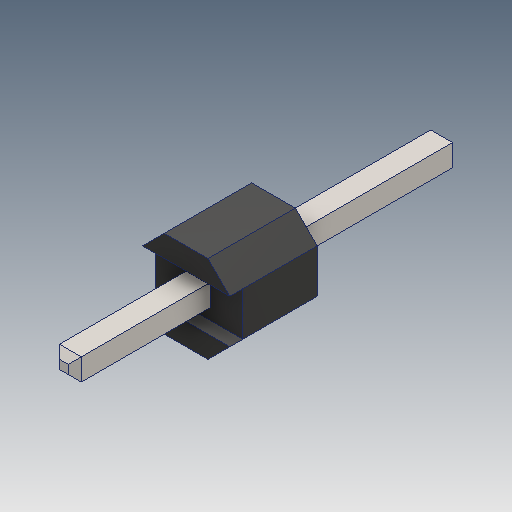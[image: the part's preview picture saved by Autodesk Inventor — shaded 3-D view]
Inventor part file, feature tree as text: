
AUTODESK INVENTOR PART (.ipt)
format: ipt  version: 2018 (Build 220112000, 112)  size: 105,472 bytes
history: native  units: mm
features: chamfer x1
ambient origin geometry x8: Origin, YZ Plane, XZ Plane, XY Plane, X Axis, Y Axis, Z Axis, Center Point
bodies: Volumenkörper1 (feature_tree)
feature tree (1):
  chamfer  "Chamfer2"  [1 undecoded]
note: 1 required parameter value undecoded (feature->parameter linkage not recoverable at this tier; creation-order binding heuristic only, values carry confidence <= 0.55)
